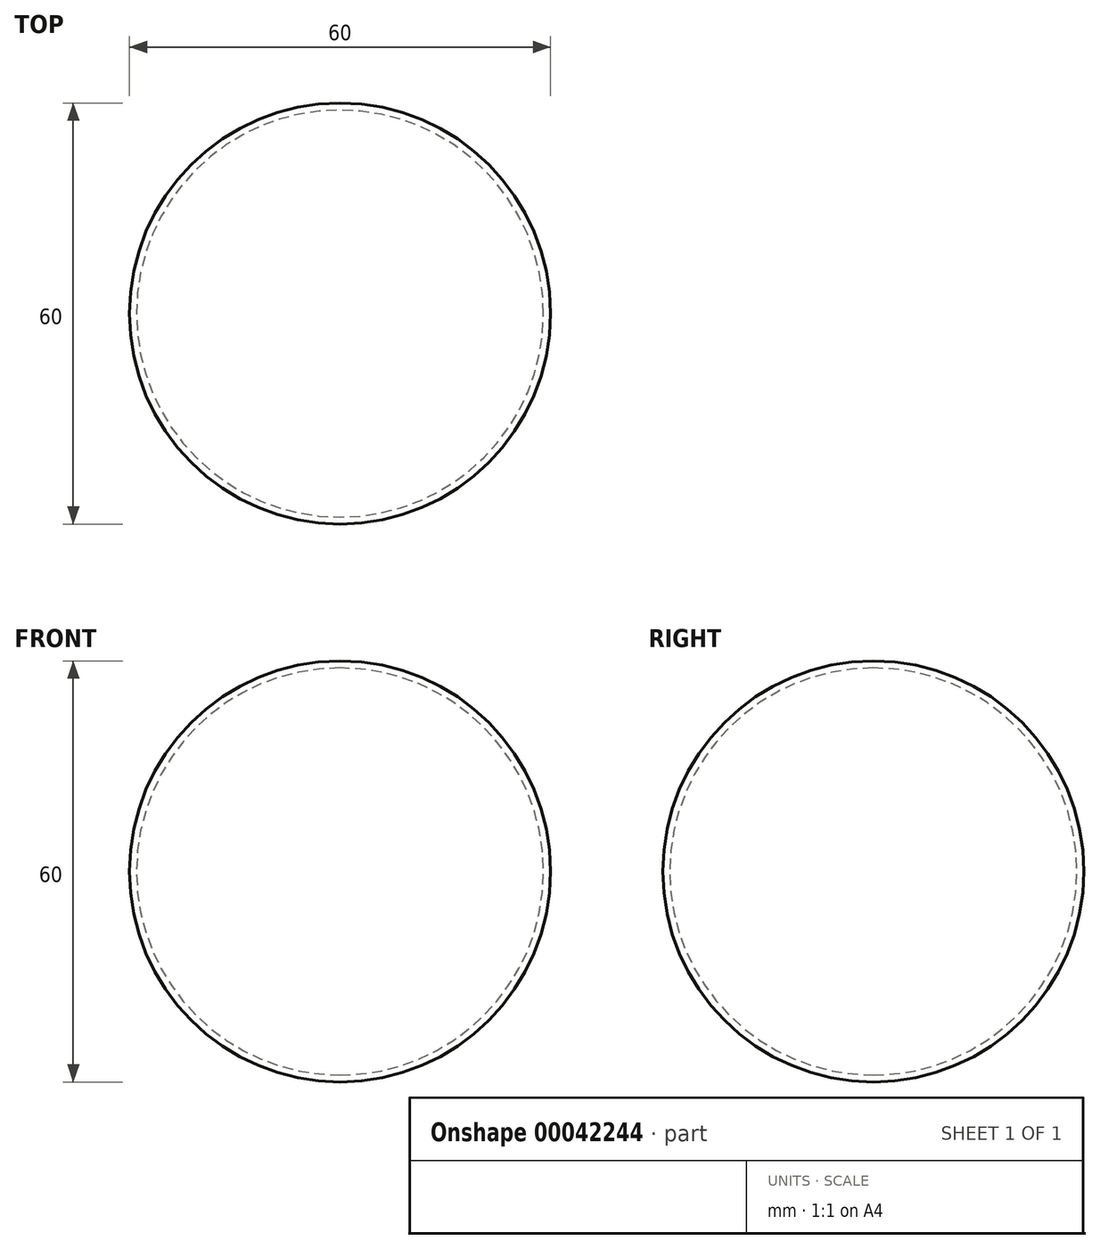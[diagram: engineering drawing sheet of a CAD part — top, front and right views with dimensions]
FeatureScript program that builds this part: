
annotation { "Feature Type Name" : "Feature", "Feature Type Description" : "" }
export const myFeature = defineFeature(function(context is Context, id is Id, definition is map)
    precondition{}
    {
        {
            var Q0;
            Q0=qCreatedBy(makeId("Front.planeOp"),FACE);
            var sketch = newSketch(context, id + "F0", { "sketchPlane" : qUnion([Q0])});
            skArc(sketch, "E0", {"start": v(0, 30) * mm, "mid": v(-30, 0) * mm, "end": v(0, -30) * mm});
            skArc(sketch, "E1.0", {"start": v(0, 29) * mm, "mid": v(-29, 0) * mm, "end": v(0, -29) * mm});
            skLineSegment(sketch, "E2", {"start": v(0, 30) * mm, "end": v(0, 29) * mm});
            skLineSegment(sketch, "E3", {"start": v(0, -30) * mm, "end": v(0, -29) * mm});
            skLineSegment(sketch, "E4", {"start": v(0, 0) * mm, "end": v(0, 23.5) * mm, "construction": true});
            skSolve(sketch);
        }
        {
            var Q0;
            Q0 = qSketchRegion(id + "F0", true);
            var Q1;
            Q1=sQuery(id+"F0.wireOp",EDGE,"E4");
            revolve(context, id + "F1", {"entities" : qUnion([Q0]), "axis" : qUnion([Q1]), "revolveType" : RevolveType.FULL});
        }
    });
